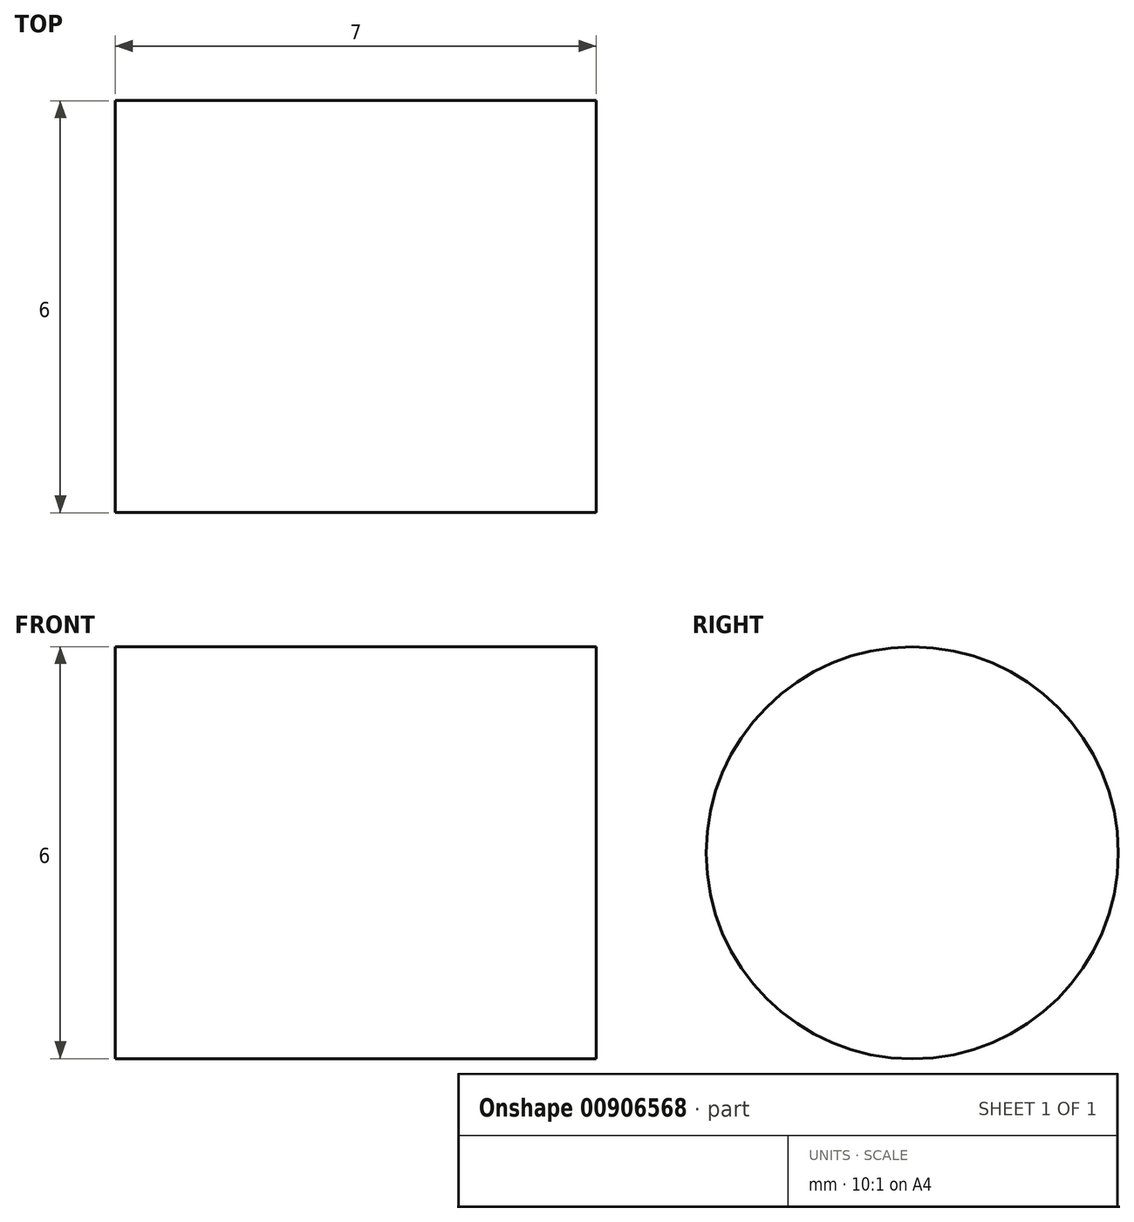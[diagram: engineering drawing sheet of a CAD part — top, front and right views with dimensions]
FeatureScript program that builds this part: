
annotation { "Feature Type Name" : "Feature", "Feature Type Description" : "" }
export const myFeature = defineFeature(function(context is Context, id is Id, definition is map)
    precondition{}
    {
        {
            var Q0;
            Q0=qCreatedBy(makeId("Right.planeOp"),FACE);
            var sketch = newSketch(context, id + "F0", { "sketchPlane" : qUnion([Q0])});
            skCircle(sketch, "E0", {"center": v(51.72, 25.19) * mm, "radius": 3 * mm});
            skSolve(sketch);
        }
        {
            var Q0;
            Q0=makeQuery(id+"F0.imprint","IMPRINT",FACE,{"disambiguationData":[TD([[makeQuery(id+"F0.imprint","IMPRINT",EDGE,{"derivedFrom":sQuery(id+"F0.wireOp",EDGE,"E0")}),1.0]])]});
            extrude(context, id + "F1", {"entities" : qUnion([Q0]), "depth" : 7 * mm, "offsetDistance" : 25.4 * mm});
        }
    });
